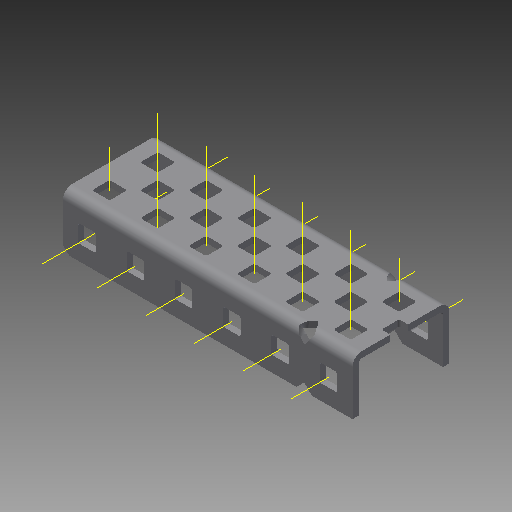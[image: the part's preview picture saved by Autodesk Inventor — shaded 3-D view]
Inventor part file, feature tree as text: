
AUTODESK INVENTOR PART (.ipt)
format: ipt  version: 2017 (Build 210142000, 142)  size: 1,869,824 bytes
history: native  units: in
note: dims shown in document units (in); Inventor stores cm internally (conversion verified against a paired STEP export)
features: other x37, pattern_linear x3, sheet_metal_op x1, extrude x1, imported_body x1, sketch x1
ambient origin geometry x8: Origin, YZ Plane, XZ Plane, XY Plane, X Axis, Y Axis, Z Axis, Center Point
bodies: Body1 (feature_tree)
feature tree (44):
  other  "C-Channel 2 x 6 (aluminum)"
  sheet_metal_op  "Fold1"
  other  "C-Channel"
  extrude  "length cut"  Depth=0.5in
  other  "top axis"
  other  "inner axis"
  other  "front axis"
  other  "back axis"
  pattern_linear  "top axes"  Spacing1=0.5in  [1 undecoded]
  pattern_linear  "inner axes"  Spacing1=0.5in  [1 undecoded]
  pattern_linear  "horiz axes"  Spacing1=-3.0in  [1 undecoded]
  other  "right plane"
  imported_body  "Base1"
  sketch  "Sketch1"  dims[d1=0.0in d4=0.5in d5=0.7874in d7=0.5in d10=0.5in d13=0.5in d14=-3.0in d15=0.0in d16=0.0in d17=0.0in d18=0.0in d19=0.0in]
  other  "Work Point1"
  other  "Work Point2"
  other  "Work Point3"
  other  "Work Point4"
  other  "Work Axis5"
  other  "Work Axis6"
  other  "Work Axis7"
  other  "Work Axis8"
  other  "Work Axis11"
  other  "Work Axis12"
  other  "Work Axis13"
  other  "Work Axis14"
  other  "Work Axis15"
  other  "Work Axis18"
  other  "Work Axis19"
  other  "Work Axis20"
  other  "Work Axis23"
  other  "Work Axis24"
  other  "Work Axis25"
  other  "Work Axis26"
  other  "Work Axis30"
  other  "Work Axis31"
  other  "Work Axis32"
  other  "Work Axis33"
  other  "left plane"
  other  "Work Axis137"
  other  "Work Axis142"
  other  "Work Axis147"
  other  "Work Axis152"
  other  "Work Axis157"
note: 3 required parameter values undecoded (feature->parameter linkage not recoverable at this tier; creation-order binding heuristic only, values carry confidence <= 0.55)
